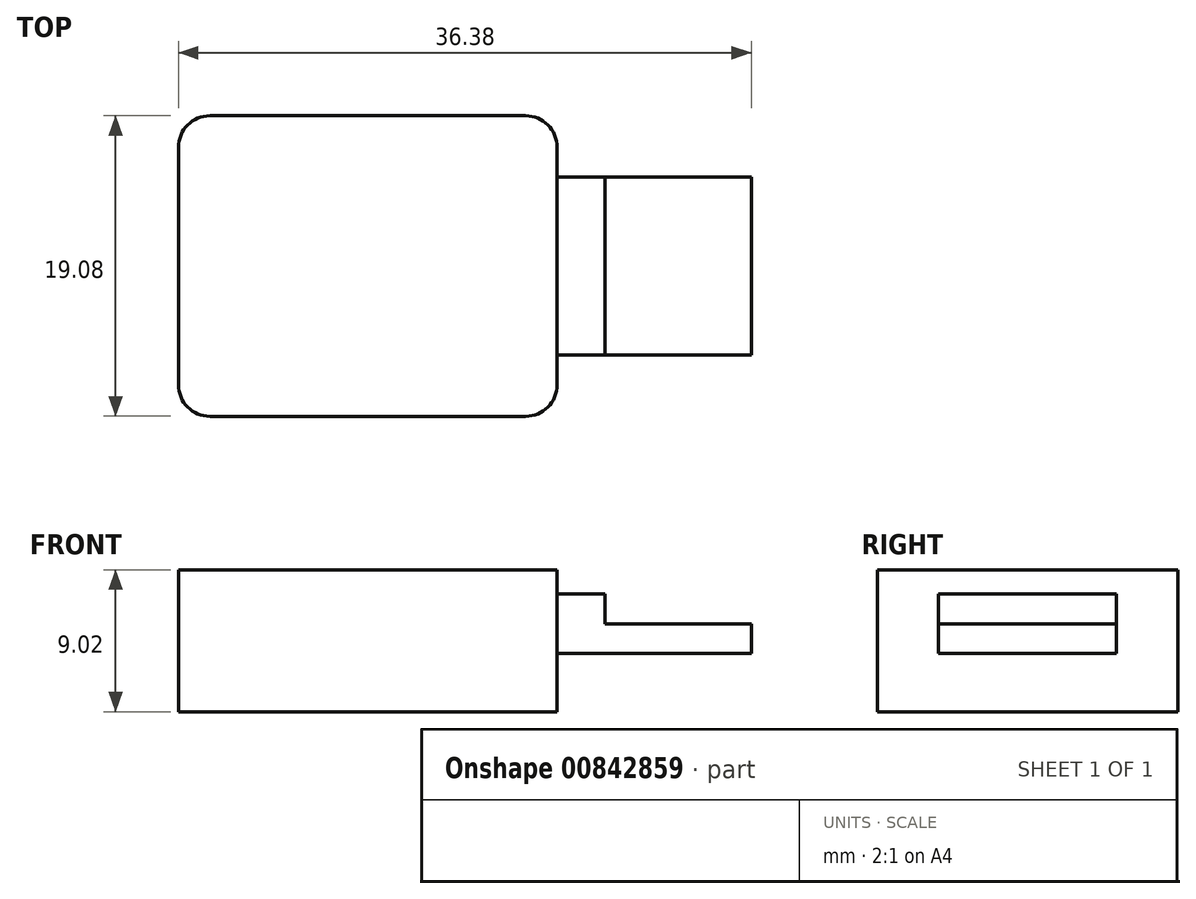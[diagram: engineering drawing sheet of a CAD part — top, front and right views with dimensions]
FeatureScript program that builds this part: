
annotation { "Feature Type Name" : "Feature", "Feature Type Description" : "" }
export const myFeature = defineFeature(function(context is Context, id is Id, definition is map)
    precondition{}
    {
        {
            var Q0;
            Q0=qCreatedBy(makeId("Top.planeOp"),FACE);
            var sketch = newSketch(context, id + "F0", { "sketchPlane" : qUnion([Q0])});
            skLineSegment(sketch, "E0.bottom", {"start": v(12.03, 9.55) * mm, "end": v(-12.03, 9.55) * mm});
            skLineSegment(sketch, "E0.top", {"start": v(12.03, -9.54) * mm, "end": v(-12.03, -9.54) * mm});
            skLineSegment(sketch, "E0.left", {"start": v(12.03, 9.55) * mm, "end": v(12.03, -9.54) * mm});
            skLineSegment(sketch, "E0.right", {"start": v(-12.02, 9.55) * mm, "end": v(-12.03, -9.54) * mm});
            skPoint(sketch, "E0.middle", {"position": v(0, 0) * mm});
            skSolve(sketch);
        }
        {
            var Q0;
            Q0 = qSketchRegion(id + "F0", true);
            extrude(context, id + "F1", {"entities" : qUnion([Q0]), "depth" : 9.02 * mm, "offsetDistance" : 25 * mm});
        }
        {
            var Q0;
            Q0=makeQuery(id+"F1.opExtrude","SWEPT_EDGE",EDGE,{"disambiguationData":[OSD([sQuery(id+"F0.wireOp",EDGE,"E0.top"),sQuery(id+"F0.wireOp",EDGE,"E0.left")])]});
            var Q1;
            Q1=makeQuery(id+"F1.opExtrude","SWEPT_EDGE",EDGE,{"disambiguationData":[OSD([sQuery(id+"F0.wireOp",EDGE,"E0.bottom"),sQuery(id+"F0.wireOp",EDGE,"E0.left")])]});
            var Q2;
            Q2=makeQuery(id+"F1.opExtrude","SWEPT_EDGE",EDGE,{"disambiguationData":[OSD([sQuery(id+"F0.wireOp",EDGE,"E0.bottom"),sQuery(id+"F0.wireOp",EDGE,"E0.right")])]});
            var Q3;
            Q3=makeQuery(id+"F1.opExtrude","SWEPT_EDGE",EDGE,{"disambiguationData":[OSD([sQuery(id+"F0.wireOp",EDGE,"E0.top"),sQuery(id+"F0.wireOp",EDGE,"E0.right")])]});
            fillet(context, id + "F2", {"entities" : qUnion([Q0, Q1, Q2, Q3]), "radius" : 2 * mm, "tangentPropagation" : true, "allowEdgeOverflow" : false});
        }
        {
            var Q0;
            Q0=makeQuery(id+"F1.opExtrude","SWEPT_FACE",FACE,{"disambiguationData":[OSD([sQuery(id+"F0.wireOp",EDGE,"E0.left")])]});
            var sketch = newSketch(context, id + "F3", { "sketchPlane" : qUnion([Q0])});
            skLineSegment(sketch, "E1", {"start": v(-5.66, 7.49) * mm, "end": v(0, 7.5) * mm});
            skLineSegment(sketch, "E2", {"start": v(-5.66, 7.49) * mm, "end": v(-5.66, 3.7) * mm});
            skLineSegment(sketch, "E3", {"start": v(-5.66, 3.7) * mm, "end": v(-5.66, 5.57) * mm});
            skLineSegment(sketch, "E4", {"start": v(-5.66, 5.57) * mm, "end": v(5.66, 5.57) * mm});
            skLineSegment(sketch, "E5.MirrorCS", {"start": v(5.66, 7.49) * mm, "end": v(0, 7.5) * mm});
            skLineSegment(sketch, "E6", {"start": v(5.66, 7.49) * mm, "end": v(5.66, 5.57) * mm});
            skSolve(sketch);
        }
        {
            var Q0;
            Q0 = qSketchRegion(id + "F3", true);
            extrude(context, id + "F4", {"entities" : qUnion([Q0]), "operationType" : NewBodyOperationType.ADD, "depth" : 3.05 * mm, "offsetDistance" : 25 * mm});
        }
        {
            var Q0;
            Q0=makeQuery(id+"F3.imprint","IMPRINT",FACE,{"disambiguationData":[TD([[makeQuery(id+"F3.imprint","IMPRINT",EDGE,{"derivedFrom":sQuery(id+"F3.wireOp",EDGE,"E1")}),1.0]])]});
            var sketch = newSketch(context, id + "F5", { "sketchPlane" : qUnion([Q0])});
            skLineSegment(sketch, "E7.0.1", {"start": v(-5.66, 5.57) * mm, "end": v(5.66, 5.57) * mm});
            skLineSegment(sketch, "E8", {"start": v(-5.66, 5.57) * mm, "end": v(-5.66, 3.7) * mm});
            skLineSegment(sketch, "E9", {"start": v(5.66, 5.57) * mm, "end": v(5.66, 3.7) * mm});
            skLineSegment(sketch, "E10", {"start": v(5.66, 3.7) * mm, "end": v(-5.66, 3.7) * mm});
            skSolve(sketch);
        }
        {
            var Q0;
            Q0 = qSketchRegion(id + "F5", true);
            extrude(context, id + "F6", {"entities" : qUnion([Q0]), "operationType" : NewBodyOperationType.ADD, "depth" : 12.33 * mm, "offsetDistance" : 25 * mm});
        }
    });
